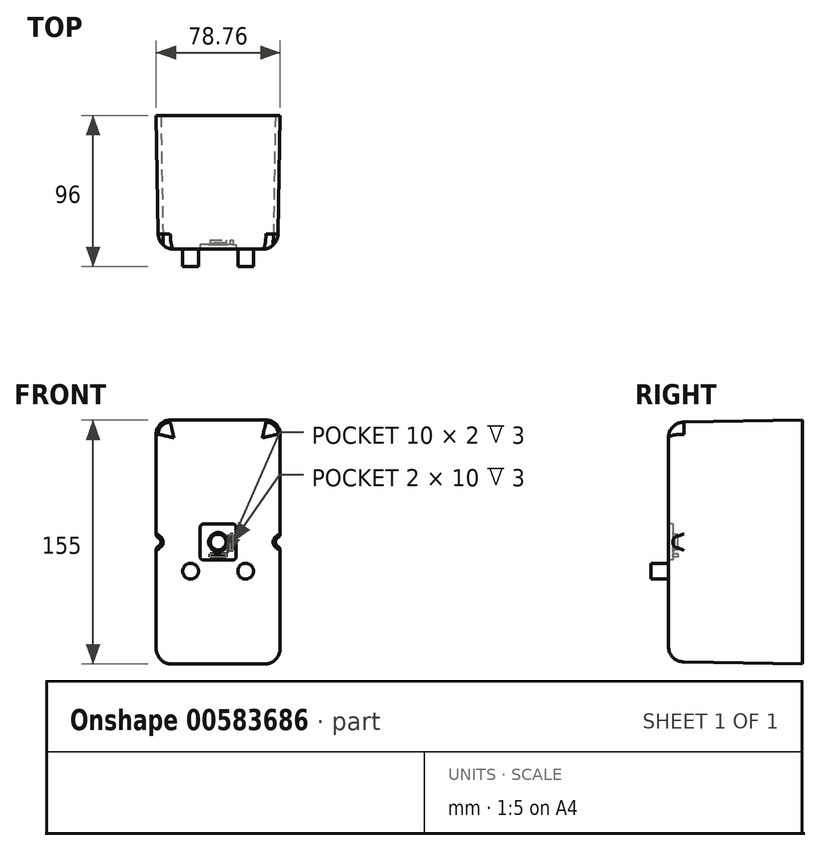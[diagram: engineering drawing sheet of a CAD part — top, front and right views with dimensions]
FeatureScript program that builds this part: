
annotation { "Feature Type Name" : "Feature", "Feature Type Description" : "" }
export const myFeature = defineFeature(function(context is Context, id is Id, definition is map)
    precondition{}
    {
        {
            var Q0;
            Q0=qCreatedBy(makeId("Front.planeOp"),FACE);
            var sketch = newSketch(context, id + "F0", { "sketchPlane" : qUnion([Q0])});
            skLineSegment(sketch, "E0.bottom", {"start": v(-30.38, 77.5) * mm, "end": v(30.38, 77.5) * mm});
            skLineSegment(sketch, "E0.top", {"start": v(-30.38, -77.5) * mm, "end": v(30.38, -77.5) * mm});
            skLineSegment(sketch, "E0.left", {"start": v(-39.37, 68.5) * mm, "end": v(-39.37, 5.2) * mm});
            skLineSegment(sketch, "E0.right", {"start": v(39.38, 68.5) * mm, "end": v(39.38, 5.2) * mm});
            skLineSegment(sketch, "E1", {"start": v(-39.38, 0) * mm, "end": v(39.38, 0) * mm, "construction": true});
            skPoint(sketch, "E2.visualSharp", {"position": v(-39.38, 77.5) * mm});
            skArc(sketch, "E2.filletArc", {"start": v(-30.38, 77.5) * mm, "mid": v(-36.74, 74.86) * mm, "end": v(-39.38, 68.5) * mm});
            skPoint(sketch, "E3.visualSharp", {"position": v(39.38, 77.5) * mm});
            skArc(sketch, "E3.filletArc", {"start": v(39.38, 68.5) * mm, "mid": v(36.74, 74.86) * mm, "end": v(30.38, 77.5) * mm});
            skPoint(sketch, "E4.visualSharp", {"position": v(39.38, -77.5) * mm});
            skArc(sketch, "E4.filletArc", {"start": v(30.38, -77.5) * mm, "mid": v(36.74, -74.86) * mm, "end": v(39.38, -68.5) * mm});
            skPoint(sketch, "E5.visualSharp", {"position": v(-39.38, -77.5) * mm});
            skArc(sketch, "E5.filletArc", {"start": v(-39.38, -68.5) * mm, "mid": v(-36.74, -74.86) * mm, "end": v(-30.38, -77.5) * mm});
            skArc(sketch, "E6", {"start": v(-37.87, -2.6) * mm, "mid": v(-36.38, 0) * mm, "end": v(-37.88, 2.6) * mm});
            skLineSegment(sketch, "E7.trimOffspring", {"start": v(-39.38, -5.2) * mm, "end": v(-39.38, -68.5) * mm});
            skPoint(sketch, "E8.visualSharp", {"position": v(-39.37, 3) * mm});
            skArc(sketch, "E8.filletArc", {"start": v(-39.38, 5.2) * mm, "mid": v(-38.97, 3.7) * mm, "end": v(-37.88, 2.6) * mm});
            skPoint(sketch, "E9.visualSharp", {"position": v(-39.37, -3) * mm});
            skArc(sketch, "E9.filletArc", {"start": v(-37.87, -2.6) * mm, "mid": v(-38.97, -3.7) * mm, "end": v(-39.38, -5.2) * mm});
            skLineSegment(sketch, "E10", {"start": v(0, 77.5) * mm, "end": v(0, -77.5) * mm, "construction": true});
            skArc(sketch, "E11.MirrorCS", {"start": v(37.88, -2.6) * mm, "mid": v(38.97, -3.7) * mm, "end": v(39.38, -5.2) * mm});
            skArc(sketch, "E12.MirrorCS", {"start": v(39.38, 5.2) * mm, "mid": v(38.97, 3.7) * mm, "end": v(37.88, 2.6) * mm});
            skArc(sketch, "E13.MirrorCS", {"start": v(37.87, -2.6) * mm, "mid": v(36.38, 0) * mm, "end": v(37.88, 2.6) * mm});
            skPoint(sketch, "E14.MirrorP", {"position": v(39.37, 3) * mm});
            skPoint(sketch, "E15.MirrorP", {"position": v(39.37, -3) * mm});
            skLineSegment(sketch, "E16.trimOffspring", {"start": v(39.38, -5.2) * mm, "end": v(39.37, -68.5) * mm});
            skSolve(sketch);
        }
        {
            var Q0;
            Q0=makeQuery(id+"F0.imprint","IMPRINT",FACE,{"disambiguationData":[TD([[makeQuery(id+"F0.imprint","IMPRINT",EDGE,{"derivedFrom":sQuery(id+"F0.wireOp",EDGE,"E0.bottom")}),-1.0]])]});
            extrude(context, id + "F1", {"entities" : qUnion([Q0]), "depth" : 85 * mm, "offsetDistance" : 25 * mm, "hasDraft" : true, "draftAngle" : 1 * degree, "draftPullDirection" : true});
        }
        {
            var Q0;
            Q0=makeQuery(id+"F1.opExtrude","CAP_FACE",FACE,{"disambiguationData":[OSD([sQuery(id+"F0.wireOp",EDGE,"E0.bottom"),sQuery(id+"F0.wireOp",EDGE,"E0.top"),sQuery(id+"F0.wireOp",EDGE,"E0.left"),sQuery(id+"F0.wireOp",EDGE,"E0.right"),sQuery(id+"F0.wireOp",EDGE,"E2.filletArc"),sQuery(id+"F0.wireOp",EDGE,"E3.filletArc"),sQuery(id+"F0.wireOp",EDGE,"E4.filletArc"),sQuery(id+"F0.wireOp",EDGE,"E5.filletArc"),sQuery(id+"F0.wireOp",EDGE,"E6"),sQuery(id+"F0.wireOp",EDGE,"E7.trimOffspring"),sQuery(id+"F0.wireOp",EDGE,"E8.filletArc"),sQuery(id+"F0.wireOp",EDGE,"E9.filletArc"),sQuery(id+"F0.wireOp",EDGE,"E11.MirrorCS"),sQuery(id+"F0.wireOp",EDGE,"E12.MirrorCS"),sQuery(id+"F0.wireOp",EDGE,"E13.MirrorCS"),sQuery(id+"F0.wireOp",EDGE,"E16.trimOffspring")])],"isStart":false});
            var sketch = newSketch(context, id + "F2", { "sketchPlane" : qUnion([Q0])});
            skLineSegment(sketch, "E17", {"start": v(0, 76.02) * mm, "end": v(0, -76.02) * mm, "construction": true});
            skPoint(sketch, "E18", {"position": v(0, 0) * mm});
            skLineSegment(sketch, "E19.bottom", {"start": v(9, 11.5) * mm, "end": v(-9, 11.5) * mm});
            skLineSegment(sketch, "E19.top", {"start": v(9, -11.5) * mm, "end": v(-9, -11.5) * mm});
            skLineSegment(sketch, "E19.left", {"start": v(11.5, 9) * mm, "end": v(11.5, -9) * mm});
            skLineSegment(sketch, "E19.right", {"start": v(-11.5, 9) * mm, "end": v(-11.5, -9) * mm});
            skPoint(sketch, "E20.visualSharp", {"position": v(11.5, 11.5) * mm});
            skArc(sketch, "E20.filletArc", {"start": v(11.5, 9) * mm, "mid": v(10.77, 10.77) * mm, "end": v(9, 11.5) * mm});
            skPoint(sketch, "E21.visualSharp", {"position": v(-11.5, 11.5) * mm});
            skArc(sketch, "E21.filletArc", {"start": v(-9, 11.5) * mm, "mid": v(-10.77, 10.77) * mm, "end": v(-11.5, 9) * mm});
            skPoint(sketch, "E22.visualSharp", {"position": v(-11.5, -11.5) * mm});
            skArc(sketch, "E22.filletArc", {"start": v(-11.5, -9) * mm, "mid": v(-10.77, -10.77) * mm, "end": v(-9, -11.5) * mm});
            skPoint(sketch, "E23.visualSharp", {"position": v(11.5, -11.5) * mm});
            skArc(sketch, "E23.filletArc", {"start": v(9, -11.5) * mm, "mid": v(10.77, -10.77) * mm, "end": v(11.5, -9) * mm});
            skCircle(sketch, "E24", {"center": v(17.5, -18.5) * mm, "radius": 5 * mm});
            skCircle(sketch, "E25", {"center": v(-17.5, -18.5) * mm, "radius": 5 * mm});
            skLineSegment(sketch, "E26", {"start": v(17.5, -18.5) * mm, "end": v(-17.5, -18.5) * mm, "construction": true});
            skPoint(sketch, "E27", {"position": v(0, -18.5) * mm});
            skLineSegment(sketch, "E28.bottom", {"start": v(5, -9.5) * mm, "end": v(-5, -9.5) * mm});
            skLineSegment(sketch, "E28.top", {"start": v(5, -7.5) * mm, "end": v(-5, -7.5) * mm});
            skLineSegment(sketch, "E28.left", {"start": v(5, -9.5) * mm, "end": v(5, -7.5) * mm});
            skLineSegment(sketch, "E28.right", {"start": v(-5, -9.5) * mm, "end": v(-5, -7.5) * mm});
            skPoint(sketch, "E28.middle", {"position": v(0, -8.5) * mm});
            skPoint(sketch, "E29", {"position": v(0, -11.5) * mm});
            skCircle(sketch, "E30", {"center": v(0, 0) * mm, "radius": 6 * mm});
            skLineSegment(sketch, "E31.1.0", {"start": v(7.5, 5) * mm, "end": v(7.5, -5) * mm});
            skLineSegment(sketch, "E31.1.1", {"start": v(9.5, -5) * mm, "end": v(7.5, -5) * mm});
            skLineSegment(sketch, "E31.1.2", {"start": v(9.5, 5) * mm, "end": v(9.5, -5) * mm});
            skLineSegment(sketch, "E31.1.3", {"start": v(9.5, 5) * mm, "end": v(7.5, 5) * mm});
            skLineSegment(sketch, "E31.anchor1", {"start": v(-5, -9.5) * mm, "end": v(0, 0) * mm, "construction": true});
            skLineSegment(sketch, "E31.anchor2", {"start": v(9.5, -5) * mm, "end": v(0, 0) * mm, "construction": true});
            skSolve(sketch);
        }
        {
            var Q0;
            Q0=makeQuery(id+"F1.opExtrude","CAP_EDGE",EDGE,{"disambiguationData":[OSD([sQuery(id+"F0.wireOp",EDGE,"E0.bottom")])],"isStart":false});
            var Q1;
            Q1=makeQuery(id+"F1.opExtrude","CAP_EDGE",EDGE,{"disambiguationData":[OSD([sQuery(id+"F0.wireOp",EDGE,"E2.filletArc")])],"isStart":false});
            var Q2;
            Q2=makeQuery(id+"F1.opExtrude","CAP_EDGE",EDGE,{"disambiguationData":[OSD([sQuery(id+"F0.wireOp",EDGE,"E0.left")])],"isStart":false});
            var Q3;
            Q3=makeQuery(id+"F1.opExtrude","CAP_EDGE",EDGE,{"disambiguationData":[OSD([sQuery(id+"F0.wireOp",EDGE,"E3.filletArc")])],"isStart":false});
            var Q4;
            Q4=makeQuery(id+"F1.opExtrude","CAP_EDGE",EDGE,{"disambiguationData":[OSD([sQuery(id+"F0.wireOp",EDGE,"E0.right")])],"isStart":false});
            fillet(context, id + "F3", {"entities" : qUnion([Q0, Q1, Q2, Q3, Q4]), "radius" : 10 * mm, "allowEdgeOverflow" : false});
        }
        {
            var Q0;
            Q0=makeQuery(id+"F2.imprint","IMPRINT",FACE,{"disambiguationData":[TD([[makeQuery(id+"F2.imprint","IMPRINT",EDGE,{"derivedFrom":sQuery(id+"F2.wireOp",EDGE,"E19.bottom")}),1.0]])]});
            var Q1;
            Q1=makeQuery(id+"F2.imprint","IMPRINT",FACE,{"disambiguationData":[TD([[makeQuery(id+"F2.imprint","IMPRINT",EDGE,{"derivedFrom":sQuery(id+"F2.wireOp",EDGE,"E30")}),1.0]])]});
            var Q2;
            Q2=makeQuery(id+"F2.imprint","IMPRINT",FACE,{"disambiguationData":[TD([[makeQuery(id+"F2.imprint","IMPRINT",EDGE,{"derivedFrom":sQuery(id+"F2.wireOp",EDGE,"E31.1.0")}),1.0]])]});
            var Q3;
            Q3=makeQuery(id+"F2.imprint","IMPRINT",FACE,{"disambiguationData":[TD([[makeQuery(id+"F2.imprint","IMPRINT",EDGE,{"derivedFrom":sQuery(id+"F2.wireOp",EDGE,"E28.bottom")}),-1.0]])]});
            extrude(context, id + "F4", {"entities" : qUnion([Q0, Q1, Q2, Q3]), "operationType" : NewBodyOperationType.REMOVE, "oppositeDirection" : true, "depth" : 3 * mm, "offsetDistance" : 25 * mm});
        }
        {
            var Q0;
            Q0=makeQuery(id+"F2.imprint","IMPRINT",FACE,{"disambiguationData":[TD([[makeQuery(id+"F2.imprint","IMPRINT",EDGE,{"derivedFrom":sQuery(id+"F2.wireOp",EDGE,"E31.1.0")}),1.0]])]});
            var Q1;
            Q1=makeQuery(id+"F2.imprint","IMPRINT",FACE,{"disambiguationData":[TD([[makeQuery(id+"F2.imprint","IMPRINT",EDGE,{"derivedFrom":sQuery(id+"F2.wireOp",EDGE,"E28.bottom")}),-1.0]])]});
            var Q2;
            Q2=makeQuery(id+"F4.boolean.opBoolean","COPY",FACE,{"derivedFrom":makeQuery(id+"F4.opExtrude","CAP_FACE",FACE,{"disambiguationData":[OSD([sQuery(id+"F2.wireOp",EDGE,"E19.bottom"),sQuery(id+"F2.wireOp",EDGE,"E19.top"),sQuery(id+"F2.wireOp",EDGE,"E19.left"),sQuery(id+"F2.wireOp",EDGE,"E19.right"),sQuery(id+"F2.wireOp",EDGE,"E20.filletArc"),sQuery(id+"F2.wireOp",EDGE,"E21.filletArc"),sQuery(id+"F2.wireOp",EDGE,"E22.filletArc"),sQuery(id+"F2.wireOp",EDGE,"E23.filletArc")])],"isStart":false})});
            extrude(context, id + "F5", {"entities" : qUnion([Q0, Q1]), "operationType" : NewBodyOperationType.REMOVE, "endBound" : BoundingType.UP_TO_SURFACE, "oppositeDirection" : true, "depth" : 3 * mm, "endBoundEntityFace" : qUnion([Q2]), "hasOffset" : true, "offsetDistance" : 3 * mm, "offsetOppositeDirection" : true});
        }
        {
            var Q0;
            Q0=makeQuery(id+"F4.boolean.opBoolean","COPY",FACE,{"derivedFrom":makeQuery(id+"F4.opExtrude","CAP_FACE",FACE,{"disambiguationData":[OSD([sQuery(id+"F2.wireOp",EDGE,"E19.bottom"),sQuery(id+"F2.wireOp",EDGE,"E19.top"),sQuery(id+"F2.wireOp",EDGE,"E19.left"),sQuery(id+"F2.wireOp",EDGE,"E19.right"),sQuery(id+"F2.wireOp",EDGE,"E20.filletArc"),sQuery(id+"F2.wireOp",EDGE,"E21.filletArc"),sQuery(id+"F2.wireOp",EDGE,"E22.filletArc"),sQuery(id+"F2.wireOp",EDGE,"E23.filletArc")])],"isStart":false})});
            var sketch = newSketch(context, id + "F6", { "sketchPlane" : qUnion([Q0])});
            skCircle(sketch, "E32", {"center": v(0, 0) * mm, "radius": 6 * mm});
            skSolve(sketch);
        }
        {
            var Q0;
            Q0 = qSketchRegion(id + "F6", true);
            var Q1;
            Q1=sQuery(id+"F6.wireOp",EDGE,"E32");
            extrude(context, id + "F7", {"entities" : qUnion([Q0]), "operationType" : NewBodyOperationType.REMOVE, "surfaceEntities" : qUnion([Q1]), "oppositeDirection" : true, "depth" : 1 * mm, "offsetDistance" : 25 * mm, "hasDraft" : true, "draftAngle" : 45 * degree, "draftPullDirection" : true});
        }
        {
            var Q0;
            Q0=makeQuery(id+"F2.imprint","IMPRINT",FACE,{"disambiguationData":[TD([[makeQuery(id+"F2.imprint","IMPRINT",EDGE,{"derivedFrom":sQuery(id+"F2.wireOp",EDGE,"E24")}),1.0]])]});
            var Q1;
            Q1=makeQuery(id+"F2.imprint","IMPRINT",FACE,{"disambiguationData":[TD([[makeQuery(id+"F2.imprint","IMPRINT",EDGE,{"derivedFrom":sQuery(id+"F2.wireOp",EDGE,"E25")}),1.0]])]});
            var Q2;
            Q2=sQuery(id+"F2.wireOp",EDGE,"E25");
            var Q3;
            Q3=sQuery(id+"F2.wireOp",EDGE,"E24");
            extrude(context, id + "F8", {"entities" : qUnion([Q0, Q1]), "operationType" : NewBodyOperationType.ADD, "surfaceEntities" : qUnion([Q2, Q3]), "depth" : 11 * mm, "offsetDistance" : 25 * mm});
        }
        {
            var Q0;
            Q0=makeQuery(id+"F1.opExtrude","CAP_EDGE",EDGE,{"disambiguationData":[OSD([sQuery(id+"F0.wireOp",EDGE,"E0.top")])],"isStart":false});
            fillet(context, id + "F9", {"entities" : qUnion([Q0]), "radius" : 10 * mm, "tangentPropagation" : true, "allowEdgeOverflow" : false});
        }
    });
